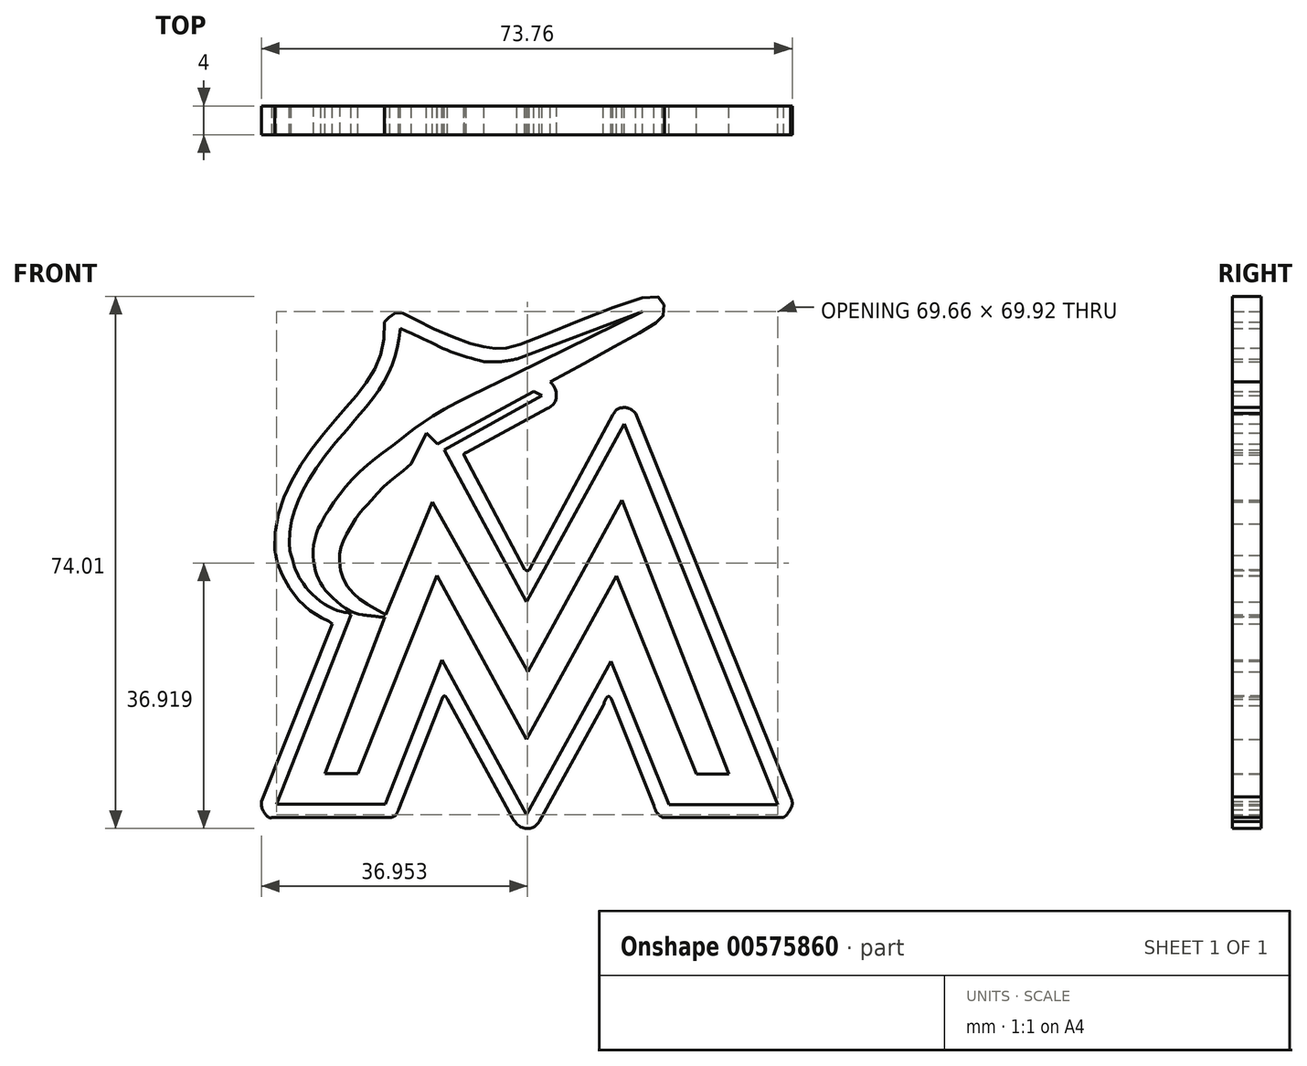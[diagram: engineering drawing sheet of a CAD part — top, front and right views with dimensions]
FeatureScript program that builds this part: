
annotation { "Feature Type Name" : "Feature", "Feature Type Description" : "" }
export const myFeature = defineFeature(function(context is Context, id is Id, definition is map)
    precondition{}
    {
        {
            var Q0;
            Q0=qCreatedBy(makeId("Front.planeOp"),FACE);
            var sketch = newSketch(context, id + "F0", { "sketchPlane" : qUnion([Q0])});
            skLineSegment(sketch, "E0", {"start": v(-35.16, -34.52) * mm, "end": v(-18.73, -34.52) * mm});
            skFitSpline(sketch, "E1", {"points": [v(-35.16, -34.52) * mm, v(-35.53, -34.52) * mm, v(-36.43, -33.42) * mm, v(-36.6, -32.29) * mm], "startDerivative": vector(-1.57, -0.47) * mm, "endDerivative": vector(0.04, 2.91) * mm});
            skLineSegment(sketch, "E2", {"start": v(-36.6, -32.29) * mm, "end": v(-26.76, -7.6) * mm});
            skFitSpline(sketch, "E3", {"points": [v(-26.76, -7.6) * mm, v(-27.12, -7.27) * mm, v(-27.63, -7.04) * mm, v(-30.6, -5.13) * mm, v(-33.38, -1.37) * mm, v(-34.65, 2.08) * mm, v(-34.08, 8.24) * mm, v(-31.22, 14.38) * mm, v(-26.76, 20.33) * mm, v(-23.13, 24.53) * mm, v(-20.32, 29.02) * mm, v(-19.5, 34.41) * mm], "startDerivative": vector(-11.35, 11.43) * mm, "endDerivative": vector(-2.07, 56.53) * mm});
            skFitSpline(sketch, "E4", {"points": [v(-19.5, 34.41) * mm, v(-19.14, 34.85) * mm, v(-18.3, 35.46) * mm, v(-17.5, 35.79) * mm, v(-15.2, 34.72) * mm, v(-8.83, 31.88) * mm, v(-5.41, 30.9) * mm, v(-3.23, 30.72) * mm, v(0, 31.51) * mm, v(16.78, 37.86) * mm, v(19.19, 37.32) * mm, v(19.29, 35.37) * mm, v(17.72, 33.96) * mm, v(3.56, 26.07) * mm], "startDerivative": vector(9.87, 16.54) * mm, "endDerivative": vector(-108.95, -58.88) * mm});
            skFitSpline(sketch, "E5", {"points": [v(3.56, 26.07) * mm, v(4.03, 25.52) * mm, v(4.33, 24.72) * mm, v(4.17, 23.23) * mm, v(3.13, 22.38) * mm], "startDerivative": vector(2.47, -2.58) * mm, "endDerivative": vector(-4.43, -2.42) * mm});
            skLineSegment(sketch, "E6", {"start": v(3.13, 22.38) * mm, "end": v(-8.16, 16.28) * mm});
            skFitSpline(sketch, "E7", {"points": [v(-8.16, 16.28) * mm, v(-8.47, 15.9) * mm], "startDerivative": vector(-0.55, -0.18) * mm, "endDerivative": vector(0.04, -0.63) * mm});
            skLineSegment(sketch, "E8", {"start": v(-8.47, 15.9) * mm, "end": v(0, 0) * mm});
            skFitSpline(sketch, "E9", {"points": [v(0, 0) * mm, v(0.27, -0.17) * mm, v(0.62, -0.1) * mm], "startDerivative": vector(0.53, -0.47) * mm, "endDerivative": vector(0.7, 0.26) * mm});
            skLineSegment(sketch, "E10", {"start": v(0.62, -0.1) * mm, "end": v(12.25, 21.53) * mm});
            skFitSpline(sketch, "E11", {"points": [v(12.25, 21.53) * mm, v(13.02, 22.36) * mm, v(13.82, 22.5) * mm, v(14.49, 22.4) * mm, v(15.42, 21.7) * mm], "startDerivative": vector(3.48, 5.9) * mm, "endDerivative": vector(3.33, -3.4) * mm});
            skLineSegment(sketch, "E12", {"start": v(15.42, 21.7) * mm, "end": v(36.92, -31.6) * mm});
            skFitSpline(sketch, "E13", {"points": [v(36.92, -31.6) * mm, v(37.14, -32.73) * mm, v(36, -34.48) * mm], "startDerivative": vector(1.26, -2.69) * mm, "endDerivative": vector(-3.42, -2.82) * mm});
            skLineSegment(sketch, "E14", {"start": v(36, -34.48) * mm, "end": v(19.12, -34.48) * mm});
            skFitSpline(sketch, "E15", {"points": [v(19.12, -34.48) * mm, v(18.92, -34.34) * mm, v(18.3, -33.75) * mm, v(17.94, -32.84) * mm], "startDerivative": vector(-0.9, 0.42) * mm, "endDerivative": vector(-0.59, 2.33) * mm});
            skLineSegment(sketch, "E16", {"start": v(17.94, -32.84) * mm, "end": v(12.02, -18.04) * mm});
            skFitSpline(sketch, "E17", {"points": [v(12.02, -18.04) * mm, v(11.87, -17.79) * mm, v(11.73, -17.66) * mm, v(11.49, -17.73) * mm, v(10.87, -18.93) * mm], "startDerivative": vector(-0.76, 1.3) * mm, "endDerivative": vector(-1.38, -3.5) * mm});
            skLineSegment(sketch, "E18", {"start": v(10.87, -18.93) * mm, "end": v(1.98, -35.08) * mm});
            skFitSpline(sketch, "E19", {"points": [v(1.98, -35.08) * mm, v(1.17, -35.88) * mm, v(-0.44, -35.88) * mm, v(-1.79, -34.43) * mm], "startDerivative": vector(-2.9, -3.6) * mm, "endDerivative": vector(-2.96, 5.31) * mm});
            skLineSegment(sketch, "E20", {"start": v(-1.79, -34.43) * mm, "end": v(-10.75, -18.03) * mm});
            skFitSpline(sketch, "E21", {"points": [v(-10.75, -18.03) * mm, v(-10.96, -17.7) * mm, v(-11.16, -17.6) * mm, v(-11.4, -17.75) * mm], "startDerivative": vector(-0.63, 0.81) * mm, "endDerivative": vector(-0.35, -1.05) * mm});
            skLineSegment(sketch, "E22", {"start": v(-11.4, -17.75) * mm, "end": v(-17.54, -33.4) * mm});
            skFitSpline(sketch, "E23", {"points": [v(-17.54, -33.4) * mm, v(-17.76, -33.93) * mm, v(-18.14, -34.32) * mm, v(-18.73, -34.52) * mm], "startDerivative": vector(-0.65, -1.77) * mm, "endDerivative": vector(-1.8, -0.35) * mm});
            skLineSegment(sketch, "E24", {"start": v(-27.76, -28.37) * mm, "end": v(-23.18, -28.37) * mm});
            skLineSegment(sketch, "E25", {"start": v(-23.18, -28.37) * mm, "end": v(-12.21, -0.82) * mm});
            skLineSegment(sketch, "E26", {"start": v(-12.21, -0.82) * mm, "end": v(0.24, -23.63) * mm});
            skLineSegment(sketch, "E27", {"start": v(0.24, -23.63) * mm, "end": v(12.75, -0.9) * mm});
            skLineSegment(sketch, "E28", {"start": v(12.75, -0.9) * mm, "end": v(23.86, -28.46) * mm});
            skLineSegment(sketch, "E29", {"start": v(23.86, -28.46) * mm, "end": v(28.38, -28.46) * mm});
            skLineSegment(sketch, "E30", {"start": v(28.38, -28.46) * mm, "end": v(13.51, 9.62) * mm});
            skLineSegment(sketch, "E31", {"start": v(13.51, 9.62) * mm, "end": v(0.4, -14.21) * mm});
            skLineSegment(sketch, "E32", {"start": v(0.4, -14.21) * mm, "end": v(-12.84, 9.37) * mm});
            skLineSegment(sketch, "E33", {"start": v(-12.84, 9.37) * mm, "end": v(-19.22, -6.07) * mm});
            skLineSegment(sketch, "E34", {"start": v(-19.22, -6.07) * mm, "end": v(-19.32, -6.3) * mm});
            skLineSegment(sketch, "E35", {"start": v(-19.32, -6.3) * mm, "end": v(-19.03, -6.55) * mm});
            skLineSegment(sketch, "E36", {"start": v(-19.03, -6.55) * mm, "end": v(-19.42, -6.64) * mm});
            skLineSegment(sketch, "E37", {"start": v(-19.42, -6.64) * mm, "end": v(-27.76, -28.37) * mm});
            skLineSegment(sketch, "E38", {"start": v(-20.44, -31.03) * mm, "end": v(-11.79, -8.95) * mm});
            skLineSegment(sketch, "E39", {"start": v(-11.79, -8.95) * mm, "end": v(0.24, -30.97) * mm});
            skLineSegment(sketch, "E40", {"start": v(0.24, -30.97) * mm, "end": v(12.29, -9.09) * mm});
            skLineSegment(sketch, "E41", {"start": v(12.29, -9.09) * mm, "end": v(21.1, -30.92) * mm});
            skLineSegment(sketch, "E42", {"start": v(21.1, -30.92) * mm, "end": v(32.65, -30.92) * mm});
            skLineSegment(sketch, "E43", {"start": v(32.65, -30.92) * mm, "end": v(13.92, 17.08) * mm});
            skLineSegment(sketch, "E44", {"start": v(13.92, 17.08) * mm, "end": v(0.24, -7.76) * mm});
            skLineSegment(sketch, "E45", {"start": v(0.24, -7.76) * mm, "end": v(-13.31, 17.05) * mm});
            skLineSegment(sketch, "E46", {"start": v(-13.31, 17.05) * mm, "end": v(-21.82, -4.66) * mm});
            skLineSegment(sketch, "E47", {"start": v(-20.44, -31.03) * mm, "end": v(-32.1, -31.03) * mm});
            skLineSegment(sketch, "E48", {"start": v(-32.1, -31.03) * mm, "end": v(-22.54, -6.33) * mm});
            skFitSpline(sketch, "E49", {"points": [v(-19.42, -6.64) * mm, v(-19.77, -6.64) * mm, v(-20.83, -6.52) * mm, v(-22.07, -6.38) * mm, v(-23.87, -6) * mm, v(-26.56, -4.1) * mm, v(-28.35, -1.98) * mm, v(-29.13, 0) * mm, v(-29.38, 3.01) * mm, v(-28.36, 6.36) * mm], "startDerivative": vector(-5.6, -0.25) * mm, "endDerivative": vector(11.2, 19.61) * mm});
            skFitSpline(sketch, "E50", {"points": [v(-28.36, 6.36) * mm, v(-27.85, 7.3) * mm, v(-25.8, 10.37) * mm, v(-21.93, 14.46) * mm, v(-17.66, 17.77) * mm, v(-12.78, 21.34) * mm, v(-1.36, 27.17) * mm], "startDerivative": vector(5.71, 11.22) * mm, "endDerivative": vector(48.16, 23.99) * mm});
            skLineSegment(sketch, "E51", {"start": v(-1.36, 27.17) * mm, "end": v(16.39, 35.84) * mm});
            skLineSegment(sketch, "E52", {"start": v(-19.37, -32.63) * mm, "end": v(-34.48, -32.63) * mm});
            skLineSegment(sketch, "E53", {"start": v(-34.48, -32.63) * mm, "end": v(-24.16, -6.31) * mm});
            skLineSegment(sketch, "E54", {"start": v(-19.37, -32.63) * mm, "end": v(-11.51, -12.57) * mm});
            skLineSegment(sketch, "E55", {"start": v(-11.51, -12.57) * mm, "end": v(0.24, -34.08) * mm});
            skLineSegment(sketch, "E56", {"start": v(0.24, -34.08) * mm, "end": v(11.97, -12.77) * mm});
            skLineSegment(sketch, "E57", {"start": v(11.97, -12.77) * mm, "end": v(20.01, -32.7) * mm});
            skLineSegment(sketch, "E58", {"start": v(20.01, -32.7) * mm, "end": v(35.18, -32.7) * mm});
            skLineSegment(sketch, "E59", {"start": v(35.18, -32.7) * mm, "end": v(13.84, 20.22) * mm});
            skLineSegment(sketch, "E60", {"start": v(13.84, 20.22) * mm, "end": v(0.23, -4.5) * mm});
            skLineSegment(sketch, "E61", {"start": v(0.23, -4.5) * mm, "end": v(-11.18, 16.6) * mm});
            skLineSegment(sketch, "E62", {"start": v(-11.18, 16.6) * mm, "end": v(2.4, 24.21) * mm});
            skLineSegment(sketch, "E63", {"start": v(2.4, 24.21) * mm, "end": v(1.25, 24.76) * mm});
            skFitSpline(sketch, "E64", {"points": [v(-15.77, 14.7) * mm, v(-16.96, 13.72) * mm, v(-19.76, 11.35) * mm, v(-22.02, 8.85) * mm, v(-22.9, 7.92) * mm, v(-24.83, 4.75) * mm, v(-25.66, 2.55) * mm, v(-25.4, -0.92) * mm, v(-23.06, -4.02) * mm, v(-19.32, -6.3) * mm], "startDerivative": vector(-14.66, -11.11) * mm, "endDerivative": vector(29.41, -15.3) * mm});
            skLineSegment(sketch, "E65", {"start": v(-21.82, -4.66) * mm, "end": v(-21.9, -4.85) * mm});
            skPoint(sketch, "E66.9.internal.snap0", {"position": v(-14.63, 17.79) * mm});
            skLineSegment(sketch, "E67", {"start": v(1.25, 24.76) * mm, "end": v(-12.14, 17.45) * mm});
            skFitSpline(sketch, "E68", {"points": [v(-23.06, -3.32) * mm, v(-23.76, -2.31) * mm, v(-24.44, -0.78) * mm, v(-24.7, 0.9) * mm, v(-24.66, 2.69) * mm, v(-23.38, 5.59) * mm, v(-21.06, 8.64) * mm, v(-16.57, 12.75) * mm], "startDerivative": vector(-7.18, 9.53) * mm, "endDerivative": vector(22.34, 19.26) * mm});
            skLineSegment(sketch, "E69", {"start": v(-23.06, -3.32) * mm, "end": v(-16.57, 12.75) * mm});
            skFitSpline(sketch, "E70", {"points": [v(-24.16, -6.31) * mm, v(-24.43, -6.06) * mm, v(-24.74, -6) * mm, v(-26.24, -5.65) * mm, v(-29.1, -3.86) * mm, v(-30.98, -1.73) * mm, v(-31.87, 0) * mm, v(-32.44, 1.94) * mm], "startDerivative": vector(-3.94, 2.79) * mm, "endDerivative": vector(-3.16, 12.19) * mm});
            skFitSpline(sketch, "E71", {"points": [v(-32.44, 1.94) * mm, v(-32.7, 2.85) * mm, v(-32.44, 6.58) * mm, v(-31.16, 10.3) * mm, v(-28.33, 15.02) * mm, v(-22.61, 21.95) * mm, v(-20.15, 25.16) * mm, v(-18.68, 27.92) * mm, v(-17.81, 30.36) * mm, v(-17.32, 33.5) * mm], "startDerivative": vector(-5.52, 13.07) * mm, "endDerivative": vector(2.65, 32.23) * mm});
            skFitSpline(sketch, "E72", {"points": [v(-17.32, 33.5) * mm, v(-17.02, 33.37) * mm, v(-13.87, 31.95) * mm, v(-9.92, 30.14) * mm, v(-5.69, 28.9) * mm], "startDerivative": vector(3.34, -1.09) * mm, "endDerivative": vector(13.71, -3.4) * mm});
            skFitSpline(sketch, "E73", {"points": [v(-5.69, 28.9) * mm, v(-3.35, 28.9) * mm, v(-1.08, 29.29) * mm], "startDerivative": vector(4.7, -0.2) * mm, "endDerivative": vector(4.52, 0.96) * mm});
            skLineSegment(sketch, "E74", {"start": v(-1.08, 29.29) * mm, "end": v(16.39, 35.84) * mm});
            skPoint(sketch, "E75.7.internal.snap0", {"position": v(6.44, 10.71) * mm});
            skPoint(sketch, "E66.6.internal.orphan", {"position": v(-28, 2.55) * mm});
            skPoint(sketch, "E66.9.internal.orphan", {"position": v(-15.19, 17.79) * mm});
            skLineSegment(sketch, "E76", {"start": v(-15.77, 14.7) * mm, "end": v(-13.67, 18.95) * mm});
            skLineSegment(sketch, "E77", {"start": v(-12.14, 17.45) * mm, "end": v(-13.67, 18.95) * mm});
            skSolve(sketch);
        }
        {
            var Q0;
            Q0=makeQuery(id+"F0.imprint","IMPRINT",FACE,{"disambiguationData":[TD([[makeQuery(id+"F0.imprint","IMPRINT",EDGE,{"derivedFrom":sQuery(id+"F0.wireOp",EDGE,"E24")}),1.0]])]});
            extrude(context, id + "F1", {"entities" : qUnion([Q0]), "depth" : 4 * mm, "offsetDistance" : 25 * mm});
        }
        {
            var Q0;
            Q0=sQuery(id+"F0.wireOp",EDGE,"E39");
            var Q1;
            Q1=sQuery(id+"F0.wireOp",EDGE,"E38");
            var Q2;
            Q2=sQuery(id+"F0.wireOp",EDGE,"E47");
            var Q3;
            Q3=sQuery(id+"F0.wireOp",EDGE,"E48");
            var Q4;
            Q4=sQuery(id+"F0.wireOp",EDGE,"E46");
            var Q5;
            Q5=sQuery(id+"F0.wireOp",EDGE,"E45");
            var Q6;
            Q6=sQuery(id+"F0.wireOp",EDGE,"E44");
            var Q7;
            Q7=sQuery(id+"F0.wireOp",EDGE,"E43");
            var Q8;
            Q8=sQuery(id+"F0.wireOp",EDGE,"E42");
            var Q9;
            Q9=sQuery(id+"F0.wireOp",EDGE,"E41");
            var Q10;
            Q10=sQuery(id+"F0.wireOp",EDGE,"E40");
            extrude(context, id + "F2", {"bodyType" : ToolBodyType.SURFACE, "surfaceEntities" : qUnion([Q0, Q1, Q2, Q3, Q4, Q5, Q6, Q7, Q8, Q9, Q10]), "depth" : 4 * mm, "offsetDistance" : 25 * mm});
        }
        {
            var Q0;
            Q0=makeQuery(id+"F0.imprint","IMPRINT",FACE,{"disambiguationData":[TD([[makeQuery(id+"F0.imprint","IMPRINT",EDGE,{"derivedFrom":sQuery(id+"F0.wireOp",EDGE,"E0")}),1.0]])]});
            extrude(context, id + "F3", {"entities" : qUnion([Q0]), "operationType" : NewBodyOperationType.ADD, "depth" : 4 * mm, "offsetDistance" : 25 * mm});
        }
        {
            var Q0;
            Q0=sQuery(id+"F0.wireOp",EDGE,"E68");
            var Q1;
            Q1=sQuery(id+"F0.wireOp",EDGE,"E69");
            extrude(context, id + "F4", {"bodyType" : ToolBodyType.SURFACE, "surfaceEntities" : qUnion([Q0, Q1]), "depth" : 4 * mm, "offsetDistance" : 25 * mm});
        }
    });
